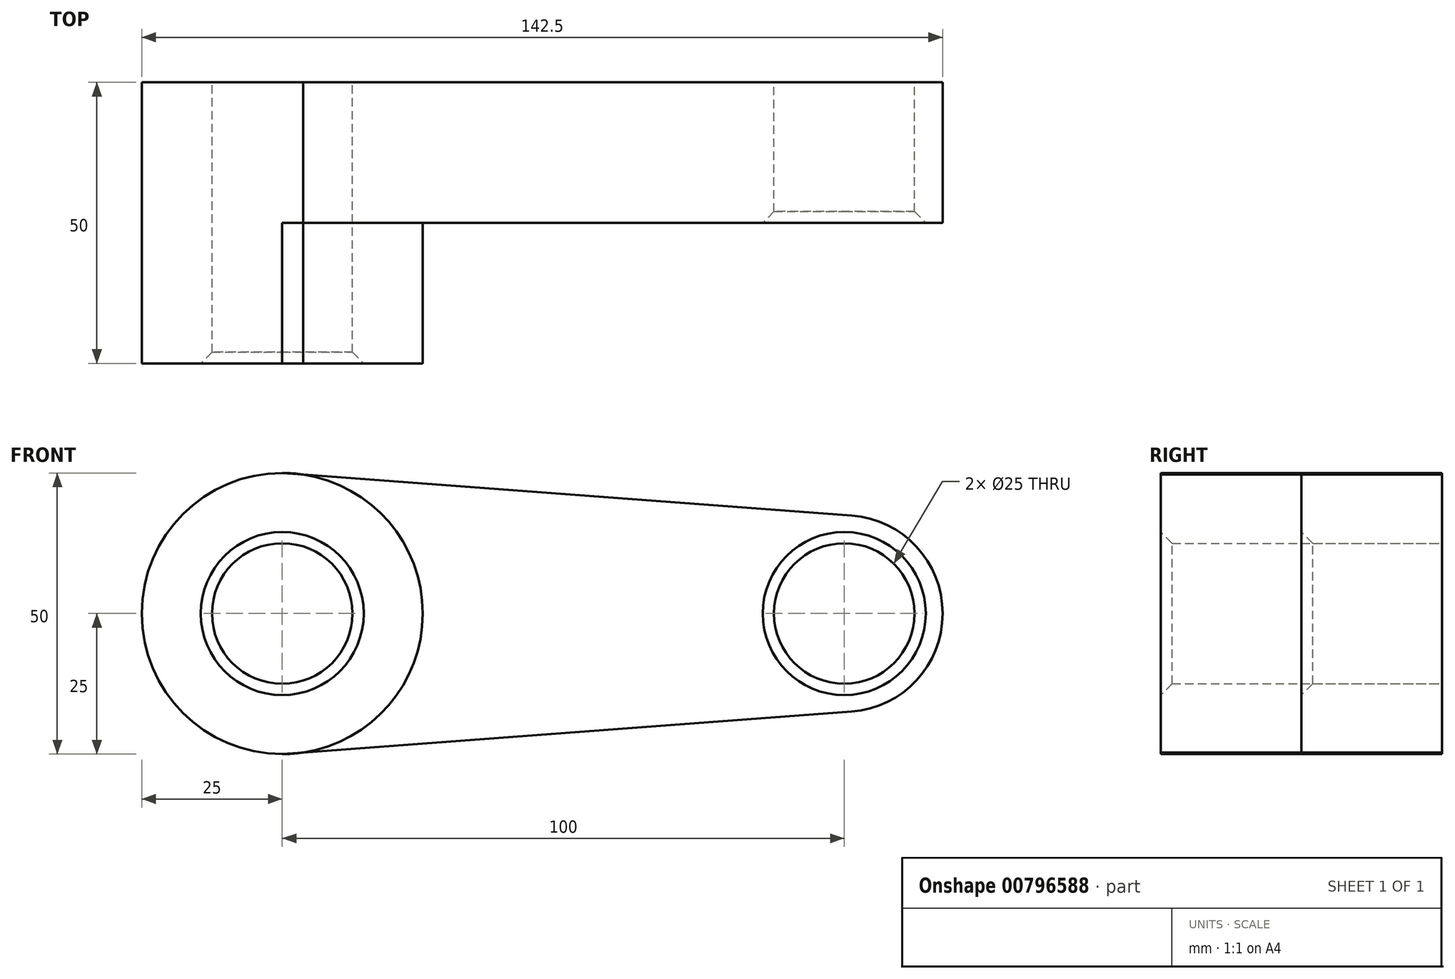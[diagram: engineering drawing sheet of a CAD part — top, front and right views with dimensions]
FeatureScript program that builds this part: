
annotation { "Feature Type Name" : "Feature", "Feature Type Description" : "" }
export const myFeature = defineFeature(function(context is Context, id is Id, definition is map)
    precondition{}
    {
        {
            var Q0;
            Q0=qCreatedBy(makeId("Front.planeOp"),FACE);
            var sketch = newSketch(context, id + "F0", { "sketchPlane" : qUnion([Q0])});
            skCircle(sketch, "E0", {"center": v(0, 0) * mm, "radius": 25 * mm});
            skCircle(sketch, "E1", {"center": v(100, 0) * mm, "radius": 17.5 * mm});
            skLineSegment(sketch, "E2", {"start": v(0, 25) * mm, "end": v(101.3, 17.45) * mm});
            skLineSegment(sketch, "E3", {"start": v(0, -25) * mm, "end": v(101.3, -17.45) * mm});
            skCircle(sketch, "E4", {"center": v(0, 0) * mm, "radius": 12.5 * mm});
            skCircle(sketch, "E5", {"center": v(100, 0) * mm, "radius": 12.5 * mm});
            skSolve(sketch);
        }
        {
            var Q0;
            Q0 = qSketchRegion(id + "F0", true);
            extrude(context, id + "F1", {"entities" : qUnion([Q0]), "depth" : 25 * mm, "offsetDistance" : 25 * mm});
        }
        {
            var Q0;
            Q0=makeQuery(id+"F0.imprint","IMPRINT",FACE,{"disambiguationData":[TD([[makeQuery(id+"F0.imprint","IMPRINT",EDGE,{"derivedFrom":sQuery(id+"F0.wireOp",EDGE,"E4")}),-1.0]])]});
            extrude(context, id + "F2", {"entities" : qUnion([Q0]), "operationType" : NewBodyOperationType.ADD, "depth" : 50 * mm, "offsetDistance" : 25 * mm});
        }
        {
            var Q0;
            Q0=makeQuery(id+"F2.opExtrude","CAP_EDGE",EDGE,{"disambiguationData":[OSD([sQuery(id+"F0.wireOp",EDGE,"E4")])],"isStart":false});
            var Q1;
            Q1=makeQuery(id+"F1.opExtrude","CAP_EDGE",EDGE,{"disambiguationData":[OSD([sQuery(id+"F0.wireOp",EDGE,"E5")])],"isStart":false});
            var Q2;
            {var subQ0=sQuery(id+"F0.wireOp",EDGE,"E0");Q2=makeQuery(id+"F2.opExtrude","CAP_EDGE",EDGE,{"disambiguationData":[OSD([subQ0]),TDD([makeQuery(id+"F0.imprint","IMPRINT",EDGE,{"disambiguationData":[TD([[makeQuery(id+"F0.imprint","INTERSECT",VERTEX,{"disambiguationData":[OD(0.0)],"derivedFrom":[subQ0,sQuery(id+"F0.wireOp",EDGE,"E2")]}),-1.0]])],"derivedFrom":subQ0})])],"isStart":false});}
            chamfer(context, id + "F3", {"entities" : qUnion([Q0, Q1, Q2]), "width" : 2 * mm, "tangentPropagation" : true});
        }
    });
